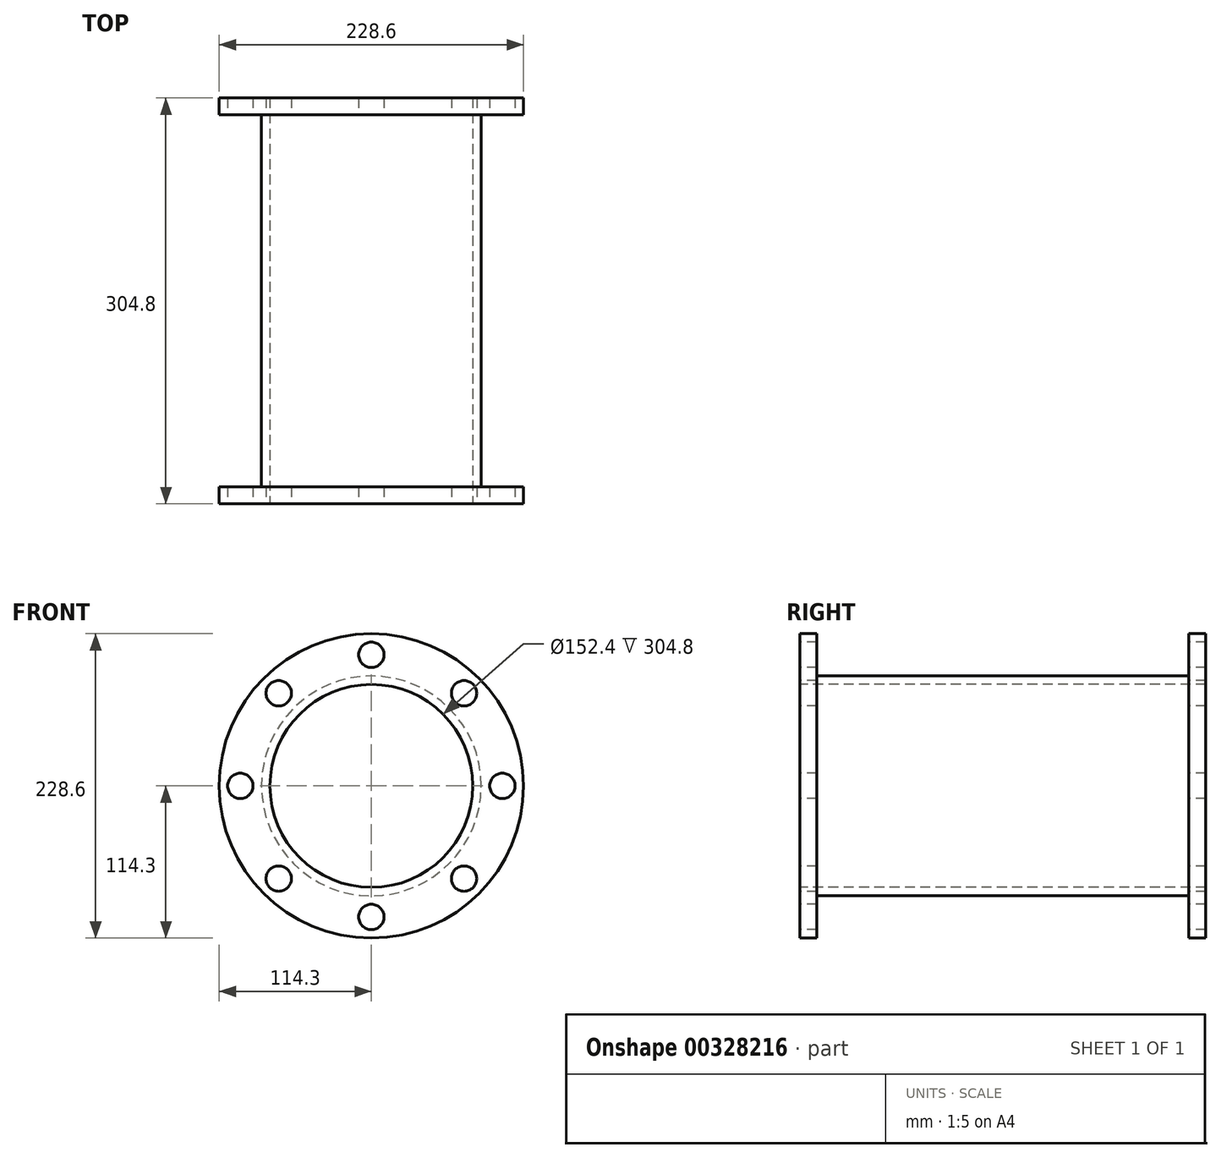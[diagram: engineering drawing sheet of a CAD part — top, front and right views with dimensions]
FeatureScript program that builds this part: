
annotation { "Feature Type Name" : "Feature", "Feature Type Description" : "" }
export const myFeature = defineFeature(function(context is Context, id is Id, definition is map)
    precondition{}
    {
        {
            var Q0;
            Q0=qCreatedBy(makeId("Right.planeOp"),FACE);
            var sketch = newSketch(context, id + "F0", { "sketchPlane" : qUnion([Q0])});
            skLineSegment(sketch, "E0", {"start": v(-372.41, 0) * mm, "end": v(512.39, 0) * mm, "construction": true});
            skLineSegment(sketch, "E1", {"start": v(0, 114.3) * mm, "end": v(-12.7, 114.3) * mm});
            skLineSegment(sketch, "E2", {"start": v(-12.7, 114.3) * mm, "end": v(-12.7, 82.55) * mm});
            skLineSegment(sketch, "E3", {"start": v(-12.7, 82.55) * mm, "end": v(-292.1, 82.55) * mm});
            skLineSegment(sketch, "E4", {"start": v(-292.1, 82.55) * mm, "end": v(-292.1, 114.3) * mm});
            skLineSegment(sketch, "E5", {"start": v(-292.1, 114.3) * mm, "end": v(-304.8, 114.3) * mm});
            skLineSegment(sketch, "E6", {"start": v(-304.8, 76.2) * mm, "end": v(0, 76.2) * mm});
            skLineSegment(sketch, "E7", {"start": v(-304.8, 114.3) * mm, "end": v(-304.8, 76.2) * mm});
            skLineSegment(sketch, "E8", {"start": v(0, 114.3) * mm, "end": v(0, 76.2) * mm});
            skSolve(sketch);
        }
        {
            var Q0;
            Q0=makeQuery(id+"F0.imprint","IMPRINT",FACE,{"disambiguationData":[TD([[makeQuery(id+"F0.imprint","IMPRINT",EDGE,{"derivedFrom":sQuery(id+"F0.wireOp",EDGE,"E1")}),1.0]])]});
            var Q1;
            Q1=sQuery(id+"F0.wireOp",EDGE,"E0");
            revolve(context, id + "F1", {"entities" : qUnion([Q0]), "axis" : qUnion([Q1]), "revolveType" : RevolveType.FULL});
        }
        {
            var Q0;
            Q0=makeQuery(id+"F1.opRevolve","SWEPT_FACE",FACE,{"disambiguationData":[OSD([sQuery(id+"F0.wireOp",EDGE,"E7")])]});
            cPlane(context, id + "F2", {"entities" : qUnion([Q0]), "cplaneType" : CPlaneType.OFFSET, "offset" : 0 * mm, "width" : 152.4 * mm, "height" : 152.4 * mm});
        }
        {
            var Q0;
            Q0=qCreatedBy(id+"F2.planeOp",FACE);
            var sketch = newSketch(context, id + "F3", { "sketchPlane" : qUnion([Q0])});
            skCircle(sketch, "E9", {"center": v(0, 0) * mm, "radius": 98.43 * mm, "construction": true});
            skCircle(sketch, "E10", {"center": v(0, 98.43) * mm, "radius": 9.53 * mm});
            skCircle(sketch, "E11.1.0", {"center": v(-69.6, 69.6) * mm, "radius": 9.53 * mm});
            skCircle(sketch, "E11.2.0", {"center": v(-98.43, 0) * mm, "radius": 9.53 * mm});
            skCircle(sketch, "E11.3.0", {"center": v(-69.6, -69.6) * mm, "radius": 9.53 * mm});
            skCircle(sketch, "E11.4.0", {"center": v(0, -98.43) * mm, "radius": 9.53 * mm});
            skCircle(sketch, "E11.5.0", {"center": v(69.6, -69.6) * mm, "radius": 9.53 * mm});
            skCircle(sketch, "E11.6.0", {"center": v(98.43, 0) * mm, "radius": 9.53 * mm});
            skCircle(sketch, "E11.7.0", {"center": v(69.6, 69.6) * mm, "radius": 9.53 * mm});
            skSolve(sketch);
        }
        {
            var Q0;
            Q0=qSketchRegion(id+"F3",true);
            extrude(context, id + "F4", {"entities" : qUnion([Q0]), "operationType" : NewBodyOperationType.REMOVE, "endBound" : BoundingType.THROUGH_ALL, "oppositeDirection" : true, "depth" : 635 * mm});
        }
    });
